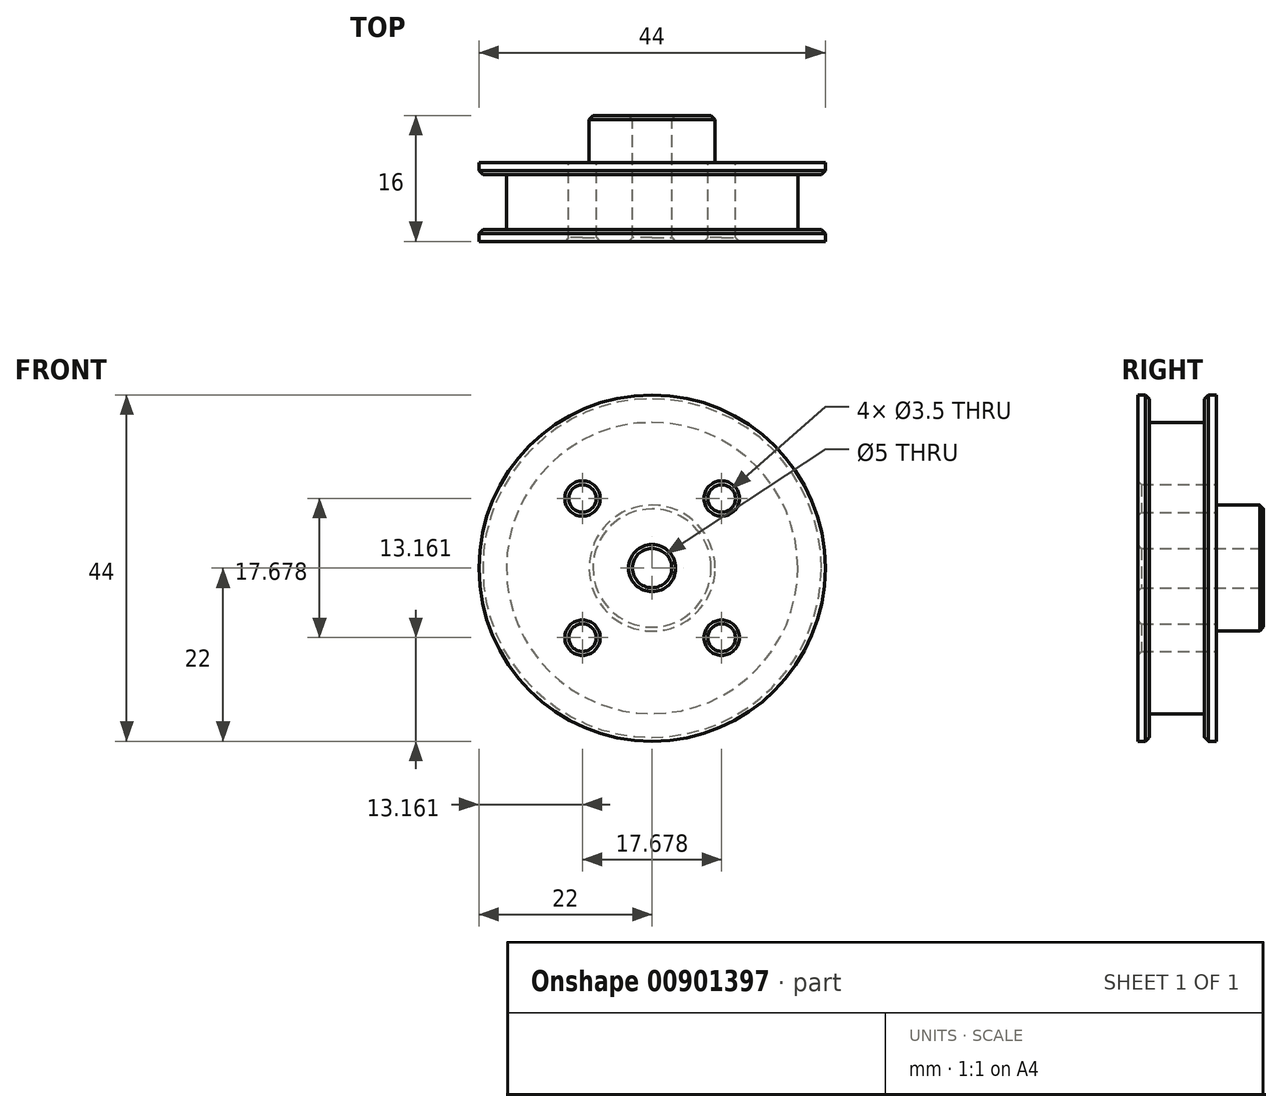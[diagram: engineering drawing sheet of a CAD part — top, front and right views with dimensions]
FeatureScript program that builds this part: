
annotation { "Feature Type Name" : "Feature", "Feature Type Description" : "" }
export const myFeature = defineFeature(function(context is Context, id is Id, definition is map)
    precondition{}
    {
        {
            var Q0;
            Q0=qCreatedBy(makeId("Front.planeOp"),FACE);
            var sketch = newSketch(context, id + "F0", { "sketchPlane" : qUnion([Q0])});
            skCircle(sketch, "E0", {"center": v(0, 0) * mm, "radius": 22 * mm});
            skSolve(sketch);
        }
        {
            var Q0;
            Q0=qSketchRegion(id+"F0",true);
            extrude(context, id + "F1", {"entities" : qUnion([Q0]), "endBound" : BoundingType.SYMMETRIC, "depth" : 10 * mm, "offsetDistance" : 25 * mm});
        }
        {
            var Q0;
            Q0=qCreatedBy(makeId("Front.planeOp"),FACE);
            var sketch = newSketch(context, id + "F2", { "sketchPlane" : qUnion([Q0])});
            skCircle(sketch, "E1", {"center": v(0, 0) * mm, "radius": 18.5 * mm});
            skCircle(sketch, "E2", {"center": v(0, 0) * mm, "radius": 30.43 * mm});
            skSolve(sketch);
        }
        {
            var Q0;
            Q0=qSketchRegion(id+"F2",true);
            extrude(context, id + "F3", {"entities" : qUnion([Q0]), "operationType" : NewBodyOperationType.REMOVE, "endBound" : BoundingType.SYMMETRIC, "depth" : 7 * mm, "offsetDistance" : 25 * mm});
        }
        {
            var Q0;
            Q0=makeQuery(id+"F1.opExtrude","CAP_FACE",FACE,{"disambiguationData":[OSD([sQuery(id+"F0.wireOp",EDGE,"E0")])],"isStart":true});
            var sketch = newSketch(context, id + "F4", { "sketchPlane" : qUnion([Q0])});
            skCircle(sketch, "E3", {"center": v(0, 0) * mm, "radius": 8 * mm});
            skSolve(sketch);
        }
        {
            var Q0;
            Q0=qSketchRegion(id+"F4",true);
            extrude(context, id + "F5", {"entities" : qUnion([Q0]), "operationType" : NewBodyOperationType.ADD, "depth" : 6 * mm, "offsetDistance" : 25 * mm});
        }
        {
            var Q0;
            Q0=makeQuery(id+"F5.opExtrude","CAP_FACE",FACE,{"disambiguationData":[OSD([sQuery(id+"F4.wireOp",EDGE,"E3")])],"isStart":false});
            var sketch = newSketch(context, id + "F6", { "sketchPlane" : qUnion([Q0])});
            skCircle(sketch, "E4", {"center": v(0, 0) * mm, "radius": 2.5 * mm});
            skSolve(sketch);
        }
        {
            var Q0;
            Q0=qSketchRegion(id+"F6",true);
            extrude(context, id + "F7", {"entities" : qUnion([Q0]), "operationType" : NewBodyOperationType.REMOVE, "endBound" : BoundingType.THROUGH_ALL, "oppositeDirection" : true, "depth" : 25 * mm, "offsetDistance" : 25 * mm});
        }
        {
            var Q0;
            Q0=makeQuery(id+"F5.opExtrude","CAP_FACE",FACE,{"disambiguationData":[OSD([sQuery(id+"F4.wireOp",EDGE,"E3")])],"isStart":false});
            var Q1;
            Q1=makeQuery(id+"F5.opExtrude","CAP_EDGE",EDGE,{"disambiguationData":[OSD([sQuery(id+"F4.wireOp",EDGE,"E3")])],"isStart":true});
            var Q2;
            Q2=makeQuery(id+"F3.boolean.opBoolean","INTERSECT",EDGE,{"derivedFrom":[makeQuery(id+"F1.opExtrude","SWEPT_FACE",FACE,{"disambiguationData":[OSD([sQuery(id+"F0.wireOp",EDGE,"E0")])]}),makeQuery(id+"F3.opExtrude","CAP_FACE",FACE,{"disambiguationData":[OSD([sQuery(id+"F2.wireOp",EDGE,"E1"),sQuery(id+"F2.wireOp",EDGE,"E2")])],"isStart":true})]});
            var Q3;
            Q3=makeQuery(id+"F3.boolean.opBoolean","INTERSECT",EDGE,{"derivedFrom":[makeQuery(id+"F1.opExtrude","SWEPT_FACE",FACE,{"disambiguationData":[OSD([sQuery(id+"F0.wireOp",EDGE,"E0")])]}),makeQuery(id+"F3.opExtrude","CAP_FACE",FACE,{"disambiguationData":[OSD([sQuery(id+"F2.wireOp",EDGE,"E1"),sQuery(id+"F2.wireOp",EDGE,"E2")])],"isStart":false})]});
            var Q4;
            Q4=makeQuery(id+"F7.boolean.opBoolean","INTERSECT",EDGE,{"derivedFrom":[makeQuery(id+"F1.opExtrude","CAP_FACE",FACE,{"disambiguationData":[OSD([sQuery(id+"F0.wireOp",EDGE,"E0")])],"isStart":false}),makeQuery(id+"F7.opExtrude","SWEPT_FACE",FACE,{"disambiguationData":[OSD([sQuery(id+"F6.wireOp",EDGE,"E4")])]})]});
            chamfer(context, id + "F8", {"entities" : qUnion([Q0, Q1, Q2, Q3, Q4]), "width" : 0.5 * mm, "tangentPropagation" : true});
        }
        {
            var Q0;
            Q0=makeQuery(id+"F1.opExtrude","CAP_FACE",FACE,{"disambiguationData":[OSD([sQuery(id+"F0.wireOp",EDGE,"E0")])],"isStart":true});
            var sketch = newSketch(context, id + "F9", { "sketchPlane" : qUnion([Q0])});
            skCircle(sketch, "E5", {"center": v(-8.84, 8.84) * mm, "radius": 1.75 * mm});
            skLineSegment(sketch, "E6", {"start": v(-22, 0) * mm, "end": v(0, 0) * mm, "construction": true});
            skLineSegment(sketch, "E7", {"start": v(0, 0) * mm, "end": v(-8.84, 8.84) * mm, "construction": true});
            skCircle(sketch, "E8.1.0", {"center": v(-8.84, -8.84) * mm, "radius": 1.75 * mm});
            skCircle(sketch, "E8.2.0", {"center": v(8.84, -8.84) * mm, "radius": 1.75 * mm});
            skCircle(sketch, "E8.3.0", {"center": v(8.84, 8.84) * mm, "radius": 1.75 * mm});
            skPoint(sketch, "E8.center", {"position": v(0, 0) * mm});
            skSolve(sketch);
        }
        {
            var Q0;
            Q0=qSketchRegion(id+"F9",true);
            extrude(context, id + "F10", {"entities" : qUnion([Q0]), "operationType" : NewBodyOperationType.REMOVE, "endBound" : BoundingType.THROUGH_ALL, "oppositeDirection" : true, "depth" : 25 * mm, "offsetDistance" : 25 * mm});
        }
        {
            var Q0;
            Q0=makeQuery(id+"F10.boolean.opBoolean","INTERSECT",EDGE,{"derivedFrom":[makeQuery(id+"F1.opExtrude","CAP_FACE",FACE,{"disambiguationData":[OSD([sQuery(id+"F0.wireOp",EDGE,"E0")])],"isStart":false}),makeQuery(id+"F10.opExtrude","SWEPT_FACE",FACE,{"disambiguationData":[OSD([sQuery(id+"F9.wireOp",EDGE,"E8.3.0")])]})]});
            var Q1;
            Q1=makeQuery(id+"F10.boolean.opBoolean","INTERSECT",EDGE,{"derivedFrom":[makeQuery(id+"F1.opExtrude","CAP_FACE",FACE,{"disambiguationData":[OSD([sQuery(id+"F0.wireOp",EDGE,"E0")])],"isStart":false}),makeQuery(id+"F10.opExtrude","SWEPT_FACE",FACE,{"disambiguationData":[OSD([sQuery(id+"F9.wireOp",EDGE,"E8.2.0")])]})]});
            var Q2;
            Q2=makeQuery(id+"F10.boolean.opBoolean","INTERSECT",EDGE,{"derivedFrom":[makeQuery(id+"F1.opExtrude","CAP_FACE",FACE,{"disambiguationData":[OSD([sQuery(id+"F0.wireOp",EDGE,"E0")])],"isStart":false}),makeQuery(id+"F10.opExtrude","SWEPT_FACE",FACE,{"disambiguationData":[OSD([sQuery(id+"F9.wireOp",EDGE,"E8.1.0")])]})]});
            var Q3;
            Q3=makeQuery(id+"F10.boolean.opBoolean","INTERSECT",EDGE,{"derivedFrom":[makeQuery(id+"F1.opExtrude","CAP_FACE",FACE,{"disambiguationData":[OSD([sQuery(id+"F0.wireOp",EDGE,"E0")])],"isStart":false}),makeQuery(id+"F10.opExtrude","SWEPT_FACE",FACE,{"disambiguationData":[OSD([sQuery(id+"F9.wireOp",EDGE,"E5")])]})]});
            var Q4;
            Q4=makeQuery(id+"F10.boolean.opBoolean","COPY",EDGE,{"derivedFrom":makeQuery(id+"F10.opExtrude","CAP_EDGE",EDGE,{"disambiguationData":[OSD([sQuery(id+"F9.wireOp",EDGE,"E5")])],"isStart":true})});
            var Q5;
            Q5=makeQuery(id+"F10.boolean.opBoolean","COPY",EDGE,{"derivedFrom":makeQuery(id+"F10.opExtrude","CAP_EDGE",EDGE,{"disambiguationData":[OSD([sQuery(id+"F9.wireOp",EDGE,"E8.3.0")])],"isStart":true})});
            var Q6;
            Q6=makeQuery(id+"F10.boolean.opBoolean","COPY",EDGE,{"derivedFrom":makeQuery(id+"F10.opExtrude","CAP_EDGE",EDGE,{"disambiguationData":[OSD([sQuery(id+"F9.wireOp",EDGE,"E8.2.0")])],"isStart":true})});
            var Q7;
            Q7=makeQuery(id+"F10.boolean.opBoolean","COPY",EDGE,{"derivedFrom":makeQuery(id+"F10.opExtrude","CAP_EDGE",EDGE,{"disambiguationData":[OSD([sQuery(id+"F9.wireOp",EDGE,"E8.1.0")])],"isStart":true})});
            chamfer(context, id + "F11", {"entities" : qUnion([Q0, Q1, Q2, Q3, Q4, Q5, Q6, Q7]), "width" : 0.5 * mm, "tangentPropagation" : true});
        }
    });
